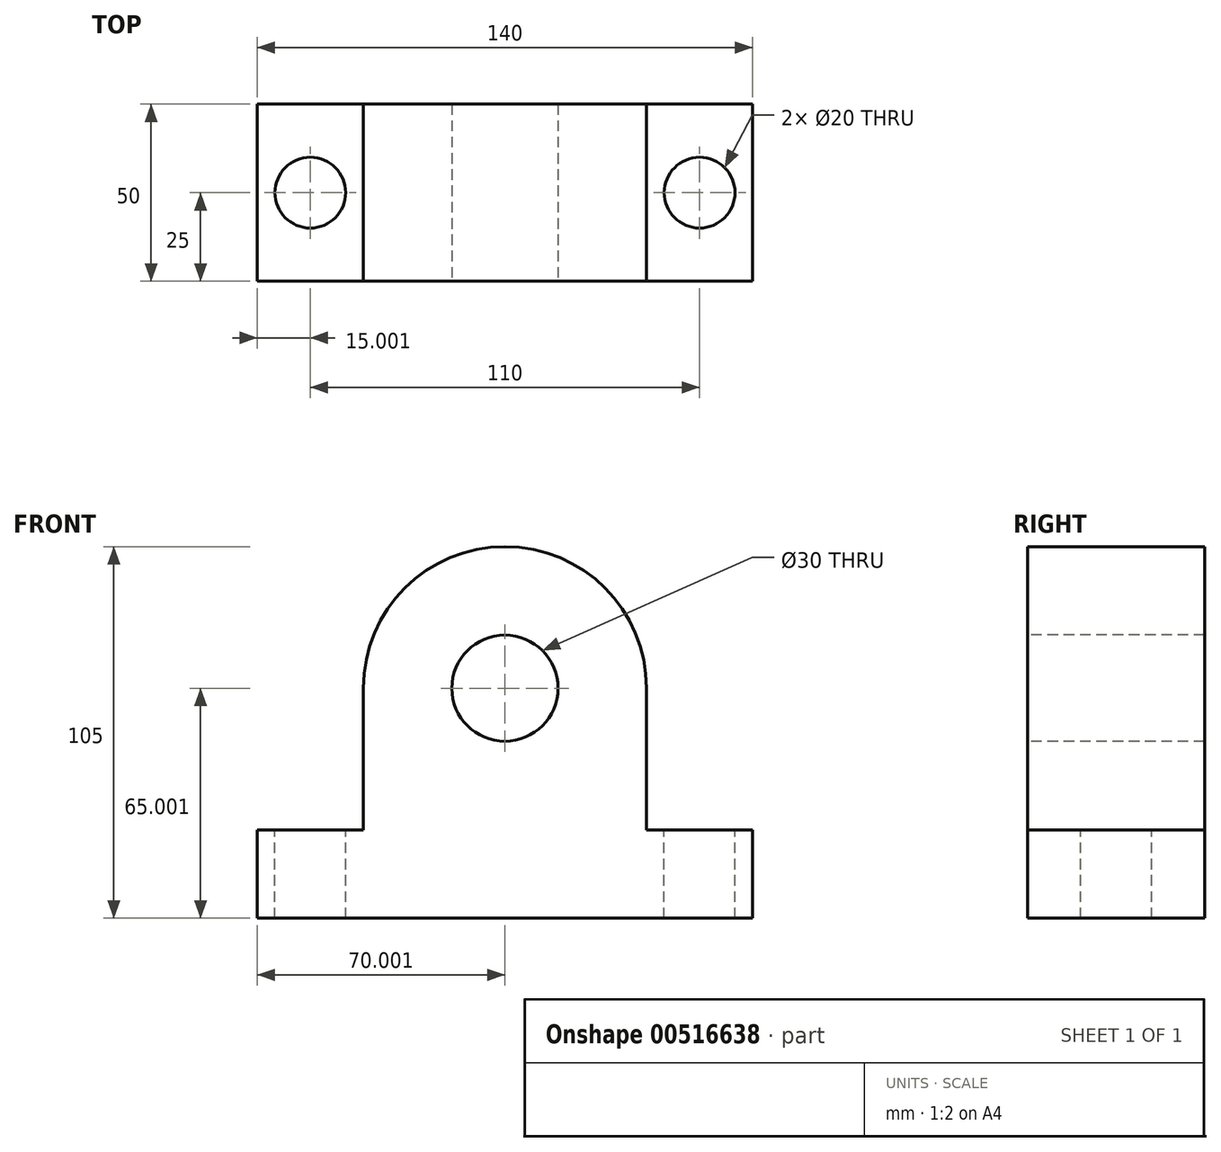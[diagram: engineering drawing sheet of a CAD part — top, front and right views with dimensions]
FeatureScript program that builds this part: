
annotation { "Feature Type Name" : "Feature", "Feature Type Description" : "" }
export const myFeature = defineFeature(function(context is Context, id is Id, definition is map)
    precondition{}
    {
        {
            var Q0;
            Q0=qCreatedBy(makeId("Front.planeOp"),FACE);
            var sketch = newSketch(context, id + "F0", { "sketchPlane" : qUnion([Q0])});
            skLineSegment(sketch, "E0", {"start": v(-73.88, -18.04) * mm, "end": v(66.12, -18.04) * mm});
            skLineSegment(sketch, "E1", {"start": v(-73.88, -18.04) * mm, "end": v(-73.88, 6.96) * mm});
            skLineSegment(sketch, "E2", {"start": v(66.12, -18.04) * mm, "end": v(66.12, 6.96) * mm});
            skLineSegment(sketch, "E3", {"start": v(-73.88, 6.96) * mm, "end": v(-43.88, 6.96) * mm});
            skLineSegment(sketch, "E4", {"start": v(66.12, 6.96) * mm, "end": v(36.12, 6.96) * mm});
            skLineSegment(sketch, "E5", {"start": v(-43.88, 6.96) * mm, "end": v(-43.88, 46.96) * mm});
            skLineSegment(sketch, "E6", {"start": v(36.12, 6.96) * mm, "end": v(36.12, 46.96) * mm});
            skArc(sketch, "E7", {"start": v(36.12, 46.96) * mm, "mid": v(-3.88, 86.96) * mm, "end": v(-43.88, 46.96) * mm});
            skSolve(sketch);
        }
        {
            var Q0;
            Q0 = qSketchRegion(id + "F0", true);
            extrude(context, id + "F1", {"entities" : qUnion([Q0]), "depth" : 50 * mm, "offsetDistance" : 25 * mm});
        }
        {
            var Q0;
            Q0=makeQuery(id+"F1.opExtrude","CAP_FACE",FACE,{"disambiguationData":[OSD([sQuery(id+"F0.wireOp",EDGE,"E0"),sQuery(id+"F0.wireOp",EDGE,"E1"),sQuery(id+"F0.wireOp",EDGE,"E2"),sQuery(id+"F0.wireOp",EDGE,"E3"),sQuery(id+"F0.wireOp",EDGE,"E4"),sQuery(id+"F0.wireOp",EDGE,"E5"),sQuery(id+"F0.wireOp",EDGE,"E6"),sQuery(id+"F0.wireOp",EDGE,"E7")])],"isStart":false});
            var sketch = newSketch(context, id + "F2", { "sketchPlane" : qUnion([Q0])});
            skCircle(sketch, "E8", {"center": v(-3.88, 46.96) * mm, "radius": 15 * mm});
            skSolve(sketch);
        }
        {
            var Q0;
            Q0 = qSketchRegion(id + "F2", true);
            extrude(context, id + "F3", {"entities" : qUnion([Q0]), "operationType" : NewBodyOperationType.REMOVE, "oppositeDirection" : true, "depth" : 50 * mm, "offsetDistance" : 25 * mm});
        }
        {
            var Q0;
            Q0=makeQuery(id+"F1.opExtrude","SWEPT_FACE",FACE,{"disambiguationData":[OSD([sQuery(id+"F0.wireOp",EDGE,"E3")])]});
            var sketch = newSketch(context, id + "F4", { "sketchPlane" : qUnion([Q0])});
            skPoint(sketch, "E9.endSnap0", {"position": v(-58.88, 0) * mm});
            skCircle(sketch, "E10", {"center": v(-58.88, -25) * mm, "radius": 10 * mm});
            skSolve(sketch);
        }
        {
            var Q0;
            Q0 = qSketchRegion(id + "F4", true);
            extrude(context, id + "F5", {"entities" : qUnion([Q0]), "operationType" : NewBodyOperationType.REMOVE, "oppositeDirection" : true, "depth" : 25 * mm, "offsetDistance" : 25 * mm});
        }
        {
            var Q0;
            Q0=makeQuery(id+"F1.opExtrude","SWEPT_FACE",FACE,{"disambiguationData":[OSD([sQuery(id+"F0.wireOp",EDGE,"E4")])]});
            var sketch = newSketch(context, id + "F6", { "sketchPlane" : qUnion([Q0])});
            skCircle(sketch, "E11", {"center": v(51.12, -25) * mm, "radius": 10 * mm});
            skSolve(sketch);
        }
        {
            var Q0;
            Q0 = qSketchRegion(id + "F6", true);
            extrude(context, id + "F7", {"entities" : qUnion([Q0]), "operationType" : NewBodyOperationType.REMOVE, "oppositeDirection" : true, "depth" : 25 * mm, "offsetDistance" : 25 * mm});
        }
    });
